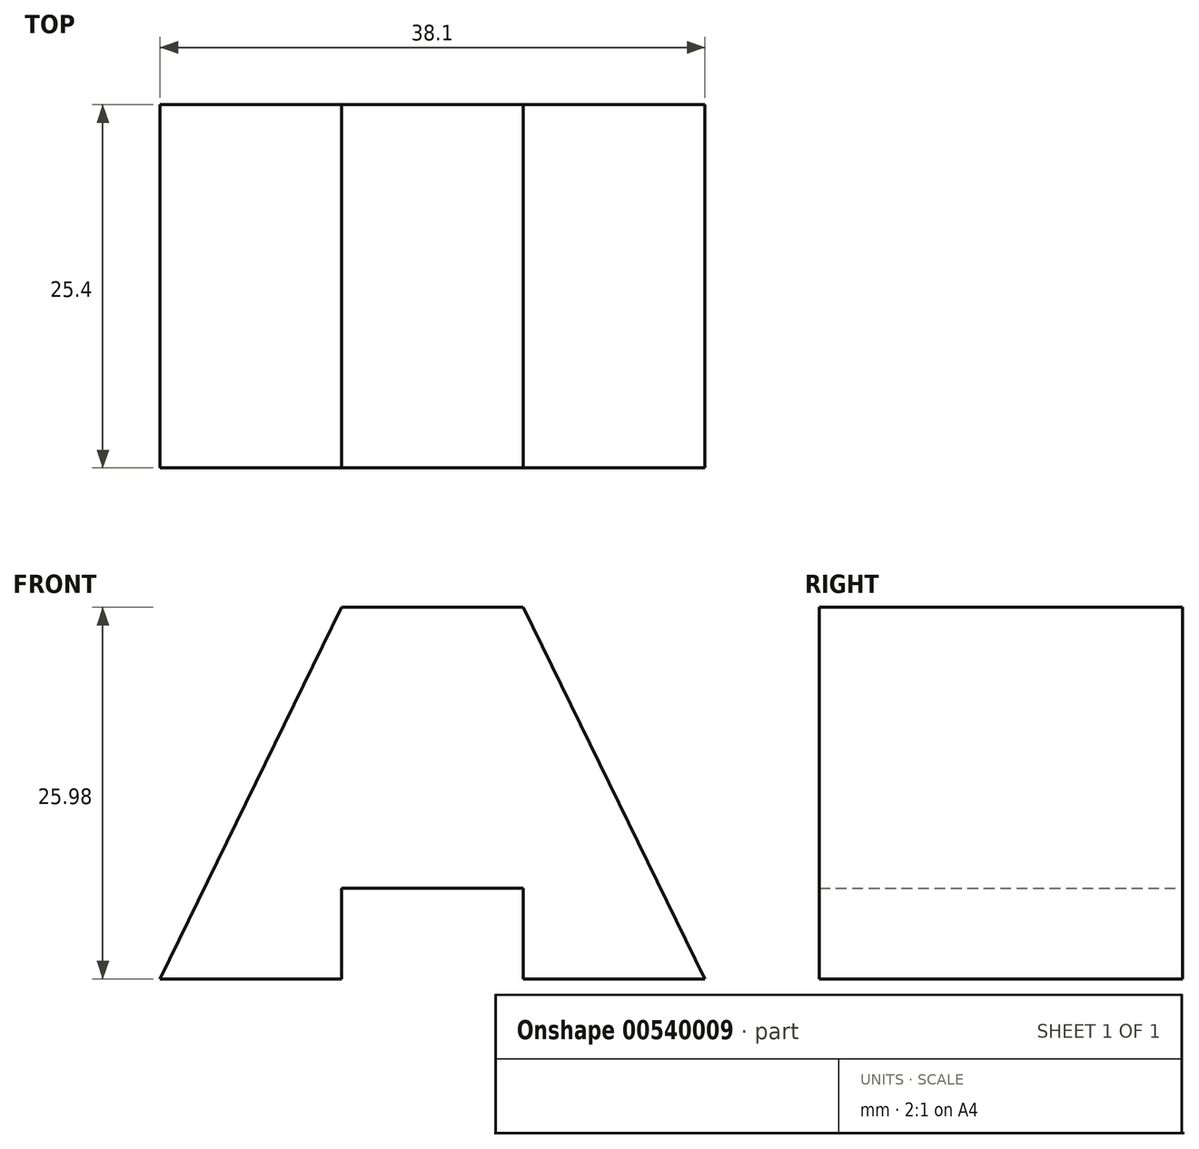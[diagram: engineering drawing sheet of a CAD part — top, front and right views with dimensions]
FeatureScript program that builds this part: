
annotation { "Feature Type Name" : "Feature", "Feature Type Description" : "" }
export const myFeature = defineFeature(function(context is Context, id is Id, definition is map)
    precondition{}
    {
        {
            var Q0;
            Q0=qCreatedBy(makeId("Front.planeOp"),FACE);
            var sketch = newSketch(context, id + "F0", { "sketchPlane" : qUnion([Q0])});
            skLineSegment(sketch, "E0", {"start": v(-63.34, 47.77) * mm, "end": v(-50.64, 47.77) * mm});
            skLineSegment(sketch, "E1", {"start": v(-63.34, 21.79) * mm, "end": v(-76.04, 21.79) * mm});
            skLineSegment(sketch, "E2", {"start": v(-50.64, 21.79) * mm, "end": v(-37.94, 21.79) * mm});
            skLineSegment(sketch, "E3", {"start": v(-50.64, 47.77) * mm, "end": v(-37.94, 21.79) * mm});
            skLineSegment(sketch, "E4", {"start": v(-63.34, 47.77) * mm, "end": v(-76.04, 21.79) * mm});
            skLineSegment(sketch, "E5", {"start": v(-63.34, 21.79) * mm, "end": v(-63.34, 28.14) * mm});
            skLineSegment(sketch, "E6", {"start": v(-63.34, 28.14) * mm, "end": v(-50.64, 28.14) * mm});
            skLineSegment(sketch, "E7", {"start": v(-50.64, 21.79) * mm, "end": v(-50.64, 28.14) * mm});
            skSolve(sketch);
        }
        {
            var Q0;
            Q0 = qSketchRegion(id + "F0", true);
            extrude(context, id + "F1", {"entities" : qUnion([Q0]), "depth" : 25.4 * mm, "offsetDistance" : 25.4 * mm});
        }
    });
